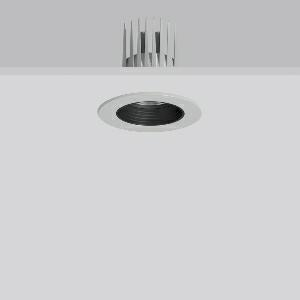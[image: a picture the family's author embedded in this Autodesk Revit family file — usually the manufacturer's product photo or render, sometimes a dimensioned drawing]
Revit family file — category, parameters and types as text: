
# Revit family: heledon_mini_e_901745_004_3_9aeb
name_source: partatom
category: Lighting Fixtures
units: mm (PartAtom-declared; Revit-internal decimal feet)

## family parameters
Cut with Voids When Loaded = No
Host = Face
Light Source = No
Part Type = Normal
Room Calculation Point = No
Round Connector Dimension = Use Diameter
Shared = No

## types (1)
- HELEDON mini E (1 x LED Modul 935, 2000 lm, 3500)
    Apparent Load = 20 VA
    Approval mark = CE
    CIE Flux Codes = 98 100 100 100 100
    Color Rendering = 92
    Color Temperature = 3500
    Default Elevation = 1800 mm
    Description = Series: HELEDON mini
Round recessed downlight. Housing: die-cast aluminium, powder-coated. Black plastic ring and recessed LED to prevent glare from the side. Optical assembly with lens made of plastic (polycarbonate) for the best homogeneous light distribution - can be changed without tools. Best colour rendering index Ra>90. Suitable for Recessed ceiling mounting. Installation without tools thanks to spring fastening system. Including separate LED converter with connecting cable 600 mm.High quality converter without flickering and stroboscopic effect. Through-wiring box (5 pole) available as accessory. The following accessories can be mounted without use of tools: interchangeable lenses, decorative glasses, honeycomb louvre, clear and frosted diffusers, white interchangeable plastic ring. 
Colour: silver
Diameter: 124 mm
Height: 3 mm
Cut-out diameter: 114 mm
Recess height: 170 mm
Luminaire: recess height: 120 mm
Lamp: LED
Socket: without socket
Colour temperature: 3500K
Colour rendering index (CRI): 92
System power: 20 W
Rated luminous flux: 2000 lm
Luminous efficiency: 100 lm/W
Control gear: Regulated power supply
Protection class: II
Type of protection: IP 20
    Height = 0 mm  [stored 0 ft]
    Lamp = 1 x LED Modul 935
    Lamp Light Flux = 2000 lm
    Lamp count = 1
    Length = 124 mm  [stored 0.406824 ft]
    Lifetime = 50000 h
    Luminous efficacy = 100 lm/W
    Manufacturer = RZB
    ModVariant = No
    Model = 901745.004.3
    Mounting Place = Ceiling
    Mounting Type = Recessed
    Number of Poles = 1
    OnlyDefault = Yes
    Power Factor = 1
    Product Name = HELEDON mini E
    Product group = Recessed downlights
    ProductGroupID = 402
    Protection Class = Protection class II
    Protection Degree = IP 20
    RLX_Detail_Level = 1
    RLX_Emergency_Light_Flux = 0 lm
    RLX_Emergency_Type = 0
    RLX_Emergency_Type_DB = No
    RlxData = <blob elided: 124953 chars, md5=ae67a5c4>
    Socket = socket
    Standby Power = 0 W
    System Light Flux = 2000 lm
    System Power = 20 W
    Type Comments = Product without accessories
    Type Image = 901656.004.jpg
    URL = http://relux.com
    VarID = ---
    Voltage = 230 V
    Voltage Range = 220-240 V
    Weight = 0.00 kg
    Width = 0 mm  [stored 0 ft]

note: [stored X ft] marks values corroborated as IEEE doubles in the binary element streams (Revit-internal decimal feet)

## geometry (parser evidence)
native form markers: Blend x4, Sweep x10
no freeform markers — native parametric forms only
